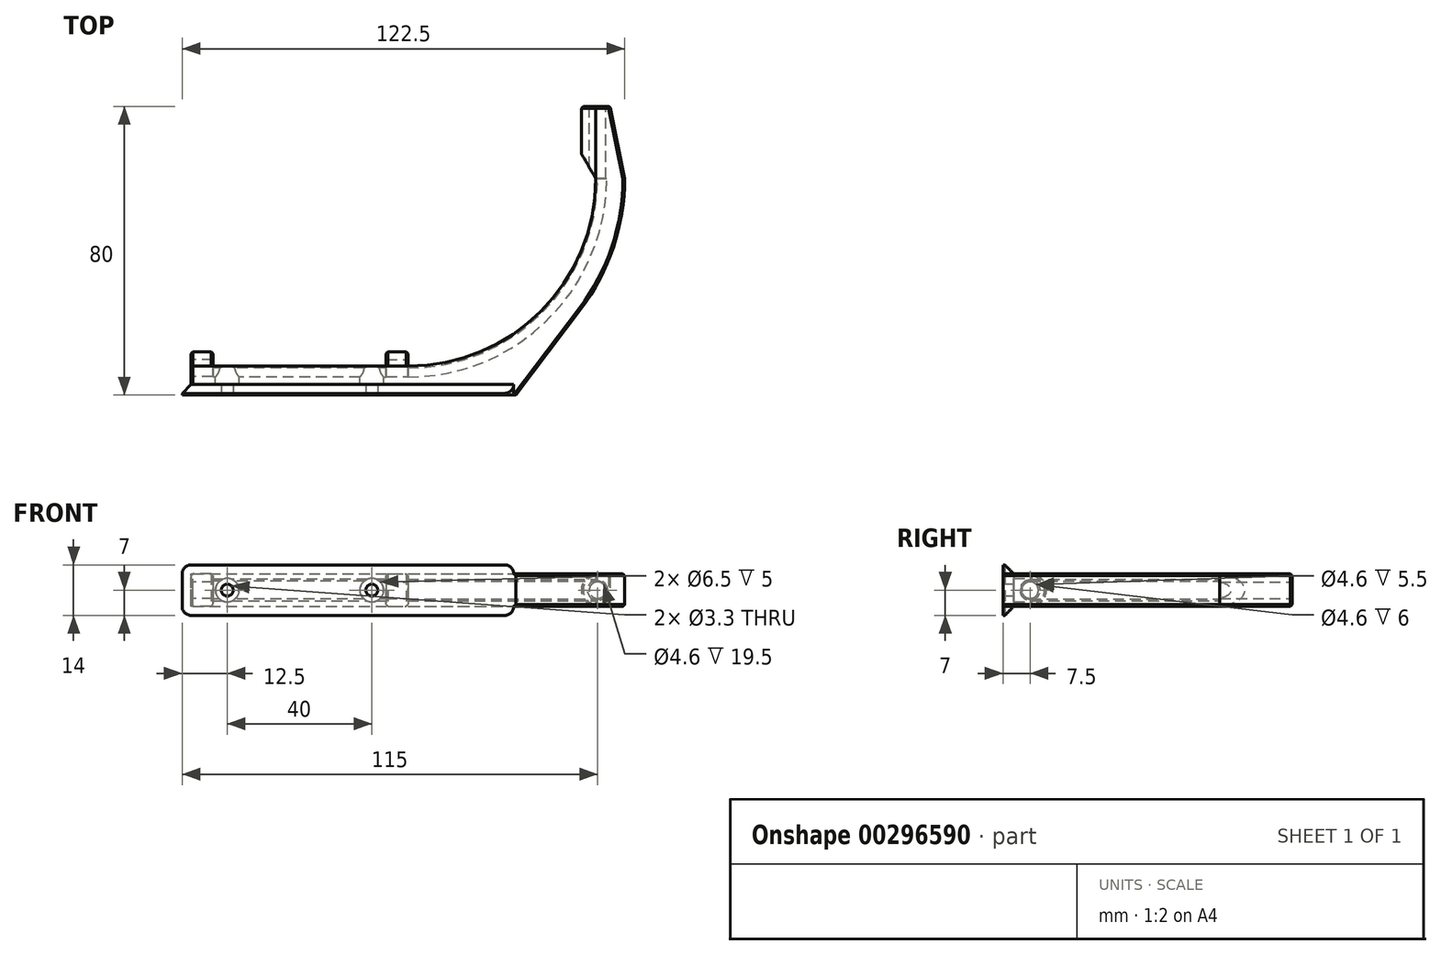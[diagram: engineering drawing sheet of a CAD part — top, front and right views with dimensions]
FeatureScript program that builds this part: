
annotation { "Feature Type Name" : "Feature", "Feature Type Description" : "" }
export const myFeature = defineFeature(function(context is Context, id is Id, definition is map)
    precondition{}
    {
        {
            var Q0;
            Q0=qCreatedBy(makeId("Top.planeOp"),FACE);
            var sketch = newSketch(context, id + "F0", { "sketchPlane" : qUnion([Q0])});
            skCircle(sketch, "E0", {"center": v(0, 120) * mm, "radius": 67 * mm, "construction": true});
            skLineSegment(sketch, "E1", {"start": v(0, 0) * mm, "end": v(0, 120) * mm, "construction": true});
            skLineSegment(sketch, "E2", {"start": v(0, 0) * mm, "end": v(-40, 0) * mm, "construction": true});
            skLineSegment(sketch, "E3", {"start": v(0, 0) * mm, "end": v(40, 0) * mm, "construction": true});
            skCircle(sketch, "E4", {"center": v(0, 120) * mm, "radius": 100 * mm, "construction": true});
            skLineSegment(sketch, "E5", {"start": v(0, 0) * mm, "end": v(50, 0) * mm});
            skArc(sketch, "E6", {"start": v(97.92, 23.9) * mm, "mid": v(106.9, 40.96) * mm, "end": v(110, 60) * mm});
            skLineSegment(sketch, "E7", {"start": v(110, 60) * mm, "end": v(110, 80) * mm});
            skLineSegment(sketch, "E8", {"start": v(0, 0) * mm, "end": v(-10, 0) * mm});
            skLineSegment(sketch, "E9.0", {"start": v(105, 60) * mm, "end": v(105, 80) * mm});
            skArc(sketch, "E9.1", {"start": v(50, 5) * mm, "mid": v(88.9, 21.1) * mm, "end": v(105, 60) * mm});
            skLineSegment(sketch, "E9.2", {"start": v(0, 5) * mm, "end": v(50, 5) * mm});
            skLineSegment(sketch, "E9.3", {"start": v(0, 5) * mm, "end": v(-10, 5) * mm});
            skLineSegment(sketch, "E10", {"start": v(-10, 5) * mm, "end": v(-10, 0) * mm});
            skLineSegment(sketch, "E11", {"start": v(105, 80) * mm, "end": v(110, 80) * mm});
            skLineSegment(sketch, "E12", {"start": v(97.92, 23.9) * mm, "end": v(79.91, 0) * mm});
            skLineSegment(sketch, "E13", {"start": v(50, 0) * mm, "end": v(79.91, 0) * mm});
            skSolve(sketch);
        }
        {
            var Q0;
            Q0 = qSketchRegion(id + "F0", true);
            extrude(context, id + "F1", {"entities" : qUnion([Q0]), "endBound" : BoundingType.SYMMETRIC, "depth" : 9 * mm});
        }
        {
            var Q0;
            Q0=makeQuery(id+"F1.opExtrude","SWEPT_FACE",FACE,{"disambiguationData":[OSD([sQuery(id+"F0.wireOp",EDGE,"E9.2"),sQuery(id+"F0.wireOp",EDGE,"E9.3")])]});
            var sketch = newSketch(context, id + "F2", { "sketchPlane" : qUnion([Q0])});
            skLineSegment(sketch, "E14", {"start": v(0, 0) * mm, "end": v(-40, 0) * mm, "construction": true});
            skPoint(sketch, "E15", {"position": v(-40, 0) * mm});
            skSolve(sketch);
        }
        {
            var Q0;
            Q0=sQuery(id+"F2.wireOp",VERTEX,"E15");
            var Q1;
            Q1=sQuery(id+"F2.wireOp",VERTEX,"E14.start");
            var Q2;
            Q2=makeQuery(id+"F1.opExtrude","SWEPT_BODY",BODY,{"disambiguationData":[OSD([sQuery(id+"F0.wireOp",EDGE,"E5"),sQuery(id+"F0.wireOp",EDGE,"E6"),sQuery(id+"F0.wireOp",EDGE,"E7"),sQuery(id+"F0.wireOp",EDGE,"E8"),sQuery(id+"F0.wireOp",EDGE,"E9.0"),sQuery(id+"F0.wireOp",EDGE,"E9.1"),sQuery(id+"F0.wireOp",EDGE,"E9.2"),sQuery(id+"F0.wireOp",EDGE,"E9.3"),sQuery(id+"F0.wireOp",EDGE,"E10"),sQuery(id+"F0.wireOp",EDGE,"E11")])]});
            hole(context, id + "F3", {"style" : HoleStyle.C_BORE, "endStyle" : HoleEndStyle.THROUGH, "standardTappedOrClearance" : lookupTablePath({ "standard" : "ISO", "fit" : "Normal", "size" : "M3", "type" : "Clearance" }), "standardBlindInLast" : lookupTablePath({ "fit" : "Standard", "standard" : "ISO", "size" : "M3", "type" : "Clearance" }), "holeDiameter" : 3.3 * mm, "cBoreDiameter" : 6.5 * mm, "cBoreDepth" : 3 * mm, "tappedDepth" : 3 * mm, "tapClearance" : 3, "startFromSketch" : true, "locations" : qUnion([Q0, Q1]), "scope" : qUnion([Q2])});
        }
        {
            var Q0;
            Q0=qCreatedBy(makeId("Top.planeOp"),FACE);
            var sketch = newSketch(context, id + "F4", { "sketchPlane" : qUnion([Q0])});
            skLineSegment(sketch, "E16", {"start": v(0, 0) * mm, "end": v(0, 5) * mm, "construction": true});
            skLineSegment(sketch, "E17", {"start": v(0, 5) * mm, "end": v(-10, 5) * mm});
            skLineSegment(sketch, "E18", {"start": v(-10, 5) * mm, "end": v(-10, 8) * mm});
            skLineSegment(sketch, "E19", {"start": v(0, 5) * mm, "end": v(50, 5) * mm});
            skArc(sketch, "E20", {"start": v(50, 5) * mm, "mid": v(88.9, 21.1) * mm, "end": v(105, 60) * mm});
            skLineSegment(sketch, "E21", {"start": v(105, 60) * mm, "end": v(105, 80) * mm});
            skLineSegment(sketch, "E22.0", {"start": v(102, 60) * mm, "end": v(102, 80) * mm});
            skArc(sketch, "E22.1", {"start": v(50, 8) * mm, "mid": v(86.77, 23.23) * mm, "end": v(102, 60) * mm});
            skLineSegment(sketch, "E22.2", {"start": v(0, 8) * mm, "end": v(50, 8) * mm});
            skLineSegment(sketch, "E22.3", {"start": v(0, 8) * mm, "end": v(-10, 8) * mm});
            skLineSegment(sketch, "E23", {"start": v(105, 80) * mm, "end": v(102, 80) * mm});
            skSolve(sketch);
        }
        {
            var Q0;
            Q0 = qSketchRegion(id + "F4", true);
            extrude(context, id + "F5", {"entities" : qUnion([Q0]), "operationType" : NewBodyOperationType.ADD, "endBound" : BoundingType.SYMMETRIC, "depth" : 9 * mm});
        }
        {
            var Q0;
            Q0=qCreatedBy(makeId("Top.planeOp"),FACE);
            var sketch = newSketch(context, id + "F6", { "sketchPlane" : qUnion([Q0])});
            skLineSegment(sketch, "E24", {"start": v(0, 0) * mm, "end": v(0, 5) * mm, "construction": true});
            skLineSegment(sketch, "E25", {"start": v(0, 5) * mm, "end": v(-11, 5) * mm});
            skLineSegment(sketch, "E26", {"start": v(0, 5) * mm, "end": v(50, 5) * mm});
            skArc(sketch, "E27", {"start": v(50, 5) * mm, "mid": v(88.9, 21.1) * mm, "end": v(105, 60) * mm});
            skLineSegment(sketch, "E28", {"start": v(105, 60) * mm, "end": v(105, 81) * mm});
            skLineSegment(sketch, "E29.0", {"start": v(0, 11) * mm, "end": v(-11, 11) * mm});
            skLineSegment(sketch, "E29.1", {"start": v(0, 11) * mm, "end": v(50, 11) * mm});
            skArc(sketch, "E29.2", {"start": v(50, 11) * mm, "mid": v(84.65, 25.35) * mm, "end": v(99, 60) * mm});
            skLineSegment(sketch, "E29.3", {"start": v(99, 60) * mm, "end": v(99, 81) * mm});
            skLineSegment(sketch, "E30", {"start": v(-11, 5) * mm, "end": v(-11, 11) * mm});
            skLineSegment(sketch, "E31", {"start": v(99, 81) * mm, "end": v(105, 81) * mm});
            skSolve(sketch);
        }
        {
            var Q0;
            Q0 = qSketchRegion(id + "F6", true);
            extrude(context, id + "F7", {"entities" : qUnion([Q0]), "operationType" : NewBodyOperationType.REMOVE, "endBound" : BoundingType.SYMMETRIC, "oppositeDirection" : true, "depth" : 5 * mm});
        }
        {
            var Q0;
            Q0=makeQuery(id+"F5.boolean.opBoolean","MERGE",FACE,{"derivedFrom":[makeQuery(id+"F1.opExtrude","SWEPT_FACE",FACE,{"disambiguationData":[OSD([sQuery(id+"F0.wireOp",EDGE,"E10")])]}),makeQuery(id+"F5.opExtrude","SWEPT_FACE",FACE,{"disambiguationData":[OSD([sQuery(id+"F4.wireOp",EDGE,"E18")])]})]});
            var sketch = newSketch(context, id + "F8", { "sketchPlane" : qUnion([Q0])});
            skLineSegment(sketch, "E32", {"start": v(0, 0) * mm, "end": v(-7.5, 0) * mm, "construction": true});
            skPoint(sketch, "E32.endSnap0", {"position": v(-5, 0) * mm});
            skCircle(sketch, "E33", {"center": v(-7.5, 0) * mm, "radius": 2.3 * mm});
            skCircle(sketch, "E34", {"center": v(-7.5, 0) * mm, "radius": 4.5 * mm});
            skSolve(sketch);
        }
        {
            var Q0;
            Q0 = qSketchRegion(id + "F8", true);
            extrude(context, id + "F9", {"entities" : qUnion([Q0]), "operationType" : NewBodyOperationType.ADD, "oppositeDirection" : true, "depth" : 6 * mm});
        }
        {
            var Q0;
            Q0=makeQuery(id+"F5.boolean.opBoolean","MERGE",FACE,{"derivedFrom":[makeQuery(id+"F1.opExtrude","SWEPT_FACE",FACE,{"disambiguationData":[OSD([sQuery(id+"F0.wireOp",EDGE,"E11")])]}),makeQuery(id+"F5.opExtrude","SWEPT_FACE",FACE,{"disambiguationData":[OSD([sQuery(id+"F4.wireOp",EDGE,"E23")])]})]});
            var sketch = newSketch(context, id + "F10", { "sketchPlane" : qUnion([Q0])});
            skLineSegment(sketch, "E35", {"start": v(-110, 0) * mm, "end": v(-102.5, 0) * mm, "construction": true});
            skPoint(sketch, "E35.endSnap0", {"position": v(-105, 0) * mm});
            skCircle(sketch, "E36", {"center": v(-102.5, 0) * mm, "radius": 2.3 * mm});
            skCircle(sketch, "E37", {"center": v(-102.5, 0) * mm, "radius": 4.5 * mm});
            skSolve(sketch);
        }
        {
            var Q0;
            Q0 = qSketchRegion(id + "F10", true);
            extrude(context, id + "F11", {"entities" : qUnion([Q0]), "operationType" : NewBodyOperationType.ADD, "oppositeDirection" : true, "depth" : 20 * mm});
        }
        {
            var Q0;
            Q0=makeQuery(id+"F7.boolean.opBoolean","INTERSECT",VERTEX,{"derivedFrom":[makeQuery(id+"F5.opExtrude","SWEPT_FACE",FACE,{"disambiguationData":[OSD([sQuery(id+"F4.wireOp",EDGE,"E22.1")])]}),makeQuery(id+"F5.opExtrude","SWEPT_FACE",FACE,{"disambiguationData":[OSD([sQuery(id+"F4.wireOp",EDGE,"E22.2"),sQuery(id+"F4.wireOp",EDGE,"E22.3")])]}),makeQuery(id+"F7.opExtrude","CAP_FACE",FACE,{"disambiguationData":[OSD([sQuery(id+"F6.wireOp",EDGE,"E25"),sQuery(id+"F6.wireOp",EDGE,"E26"),sQuery(id+"F6.wireOp",EDGE,"E27"),sQuery(id+"F6.wireOp",EDGE,"E28"),sQuery(id+"F6.wireOp",EDGE,"E29.0"),sQuery(id+"F6.wireOp",EDGE,"E29.1"),sQuery(id+"F6.wireOp",EDGE,"E29.2"),sQuery(id+"F6.wireOp",EDGE,"E29.3"),sQuery(id+"F6.wireOp",EDGE,"E30"),sQuery(id+"F6.wireOp",EDGE,"E31")])],"isStart":false})]});
            var Q1;
            Q1=makeQuery(id+"F7.boolean.opBoolean","INTERSECT",VERTEX,{"derivedFrom":[makeQuery(id+"F5.opExtrude","SWEPT_FACE",FACE,{"disambiguationData":[OSD([sQuery(id+"F4.wireOp",EDGE,"E22.1")])]}),makeQuery(id+"F5.opExtrude","SWEPT_FACE",FACE,{"disambiguationData":[OSD([sQuery(id+"F4.wireOp",EDGE,"E22.2"),sQuery(id+"F4.wireOp",EDGE,"E22.3")])]}),makeQuery(id+"F7.opExtrude","CAP_FACE",FACE,{"disambiguationData":[OSD([sQuery(id+"F6.wireOp",EDGE,"E25"),sQuery(id+"F6.wireOp",EDGE,"E26"),sQuery(id+"F6.wireOp",EDGE,"E27"),sQuery(id+"F6.wireOp",EDGE,"E28"),sQuery(id+"F6.wireOp",EDGE,"E29.0"),sQuery(id+"F6.wireOp",EDGE,"E29.1"),sQuery(id+"F6.wireOp",EDGE,"E29.2"),sQuery(id+"F6.wireOp",EDGE,"E29.3"),sQuery(id+"F6.wireOp",EDGE,"E30"),sQuery(id+"F6.wireOp",EDGE,"E31")])],"isStart":true})]});
            var Q2;
            Q2=makeQuery(id+"F7.boolean.opBoolean","COPY",VERTEX,{"derivedFrom":makeQuery(id+"F7.opExtrude","CAP_VERTEX",VERTEX,{"disambiguationData":[OSD([sQuery(id+"F6.wireOp",EDGE,"E26"),sQuery(id+"F6.wireOp",EDGE,"E27")])],"isStart":false})});
            cPlane(context, id + "F12", {"entities" : qUnion([Q0, Q1, Q2]), "cplaneType" : CPlaneType.THREE_POINT, "offset" : 25 * mm, "width" : 150 * mm, "height" : 150 * mm});
        }
        {
            var Q0;
            Q0=qCreatedBy(id+"F12.planeOp",FACE);
            var sketch = newSketch(context, id + "F13", { "sketchPlane" : qUnion([Q0])});
            skLineSegment(sketch, "E38", {"start": v(-7.5, 0) * mm, "end": v(0, 0) * mm, "construction": true});
            skCircle(sketch, "E39", {"center": v(-7.5, 0) * mm, "radius": 2.3 * mm});
            skCircle(sketch, "E40", {"center": v(-7.5, 0) * mm, "radius": 4.5 * mm});
            skSolve(sketch);
        }
        {
            var Q0;
            Q0 = qSketchRegion(id + "F13", true);
            extrude(context, id + "F14", {"entities" : qUnion([Q0]), "operationType" : NewBodyOperationType.ADD, "depth" : 6 * mm});
        }
        {
            var Q0;
            {var subQ1=sQuery(id+"F0.wireOp",EDGE,"E10");var subQ2=sQuery(id+"F4.wireOp",EDGE,"E22.3");var subQ3=sQuery(id+"F4.wireOp",EDGE,"E22.2");Q0=makeQuery(id+"F7.boolean.opBoolean","SPLIT",FACE,{"disambiguationData":[TD([makeQuery(id+"F1.opExtrude","CAP_FACE",FACE,{"disambiguationData":[OSD([sQuery(id+"F0.wireOp",EDGE,"E5"),sQuery(id+"F0.wireOp",EDGE,"E6"),sQuery(id+"F0.wireOp",EDGE,"E7"),sQuery(id+"F0.wireOp",EDGE,"E8"),sQuery(id+"F0.wireOp",EDGE,"E9.0"),sQuery(id+"F0.wireOp",EDGE,"E9.1"),sQuery(id+"F0.wireOp",EDGE,"E9.2"),sQuery(id+"F0.wireOp",EDGE,"E9.3"),subQ1,sQuery(id+"F0.wireOp",EDGE,"E11")])],"isStart":true})])],"derivedFrom":makeQuery(id+"F5.opExtrude","SWEPT_FACE",FACE,{"disambiguationData":[OSD([subQ3,subQ2])]})});}
            var sketch = newSketch(context, id + "F15", { "sketchPlane" : qUnion([Q0])});
            skLineSegment(sketch, "E41", {"start": v(0, 0) * mm, "end": v(-40, 0) * mm, "construction": true});
            skCircle(sketch, "E42", {"center": v(-40, 0) * mm, "radius": 3.25 * mm});
            skCircle(sketch, "E43", {"center": v(0, 0) * mm, "radius": 3.25 * mm});
            skSolve(sketch);
        }
        {
            var Q0;
            Q0 = qSketchRegion(id + "F15", true);
            extrude(context, id + "F16", {"entities" : qUnion([Q0]), "operationType" : NewBodyOperationType.REMOVE, "oppositeDirection" : true, "depth" : 3 * mm});
        }
        {
            var Q0;
            Q0=makeQuery(id+"F5.boolean.opBoolean","MERGE",FACE,{"derivedFrom":[makeQuery(id+"F1.opExtrude","CAP_FACE",FACE,{"disambiguationData":[OSD([sQuery(id+"F0.wireOp",EDGE,"E5"),sQuery(id+"F0.wireOp",EDGE,"E6"),sQuery(id+"F0.wireOp",EDGE,"E7"),sQuery(id+"F0.wireOp",EDGE,"E8"),sQuery(id+"F0.wireOp",EDGE,"E9.0"),sQuery(id+"F0.wireOp",EDGE,"E9.1"),sQuery(id+"F0.wireOp",EDGE,"E9.2"),sQuery(id+"F0.wireOp",EDGE,"E9.3"),sQuery(id+"F0.wireOp",EDGE,"E10"),sQuery(id+"F0.wireOp",EDGE,"E11"),sQuery(id+"F0.wireOp",EDGE,"E12"),sQuery(id+"F0.wireOp",EDGE,"E13")])],"isStart":false}),makeQuery(id+"F5.opExtrude","CAP_FACE",FACE,{"disambiguationData":[OSD([sQuery(id+"F4.wireOp",EDGE,"E17"),sQuery(id+"F4.wireOp",EDGE,"E18"),sQuery(id+"F4.wireOp",EDGE,"E19"),sQuery(id+"F4.wireOp",EDGE,"E20"),sQuery(id+"F4.wireOp",EDGE,"E21"),sQuery(id+"F4.wireOp",EDGE,"E22.0"),sQuery(id+"F4.wireOp",EDGE,"E22.1"),sQuery(id+"F4.wireOp",EDGE,"E22.2"),sQuery(id+"F4.wireOp",EDGE,"E22.3"),sQuery(id+"F4.wireOp",EDGE,"E23")])],"isStart":false})]});
            var sketch = newSketch(context, id + "F17", { "sketchPlane" : qUnion([Q0])});
            skLineSegment(sketch, "E44", {"start": v(0, 0) * mm, "end": v(102, 0) * mm, "construction": true});
            skLineSegment(sketch, "E45", {"start": v(102, 0) * mm, "end": v(102, 60) * mm, "construction": true});
            skLineSegment(sketch, "E46", {"start": v(102, 60) * mm, "end": v(96, 60) * mm});
            skLineSegment(sketch, "E47", {"start": v(96, 60) * mm, "end": v(96, 70.4) * mm});
            skLineSegment(sketch, "E48", {"start": v(96, 70.4) * mm, "end": v(102, 60) * mm});
            skSolve(sketch);
        }
        {
            var Q0;
            Q0 = qSketchRegion(id + "F17", true);
            extrude(context, id + "F18", {"entities" : qUnion([Q0]), "operationType" : NewBodyOperationType.REMOVE, "endBound" : BoundingType.THROUGH_ALL, "oppositeDirection" : true, "depth" : 25 * mm});
        }
        {
            var Q0;
            {var subQ0=sQuery(id+"F6.wireOp",EDGE,"E27");var subQ1=sQuery(id+"F6.wireOp",EDGE,"E26");var subQ2=sQuery(id+"F6.wireOp",EDGE,"E25");var subQ3=makeQuery(id+"F7.opExtrude","CAP_FACE",FACE,{"disambiguationData":[OSD([subQ2,subQ1,subQ0,sQuery(id+"F6.wireOp",EDGE,"E28"),sQuery(id+"F6.wireOp",EDGE,"E29.0"),sQuery(id+"F6.wireOp",EDGE,"E29.1"),sQuery(id+"F6.wireOp",EDGE,"E29.2"),sQuery(id+"F6.wireOp",EDGE,"E29.3"),sQuery(id+"F6.wireOp",EDGE,"E30"),sQuery(id+"F6.wireOp",EDGE,"E31")])],"isStart":false});var subQ4=makeQuery(id+"F7.opExtrude","SWEPT_FACE",FACE,{"disambiguationData":[OSD([subQ2,subQ1])]});Q0=makeQuery(id+"F7.boolean.opBoolean","COPY",EDGE,{"disambiguationData":[topologyDisambiguationEdgeConnected([subQ4,subQ3]),TD([makeQuery(id+"F3.hole-0.boolean.opBoolean","COPY",FACE,{"derivedFrom":makeQuery(id+"F3.hole-0.opRevolve","SWEPT_FACE",FACE,{"disambiguationData":[OSD([sQuery(id+"F3.hole-0.sketch.wireOp",EDGE,"cbore_start_line_2")])]})}),makeQuery(id+"F5.opExtrude","SWEPT_FACE",FACE,{"disambiguationData":[OSD([sQuery(id+"F4.wireOp",EDGE,"E17"),sQuery(id+"F4.wireOp",EDGE,"E19")])]}),subQ4,subQ3,makeQuery(id+"F7.opExtrude","SWEPT_FACE",FACE,{"disambiguationData":[OSD([subQ0])]})])],"derivedFrom":makeQuery(id+"F7.opExtrude","CAP_EDGE",EDGE,{"disambiguationData":[OSD([subQ2,subQ1])],"isStart":false})});}
            var Q1;
            {var subQ0=sQuery(id+"F6.wireOp",EDGE,"E27");var subQ1=sQuery(id+"F6.wireOp",EDGE,"E26");var subQ2=sQuery(id+"F6.wireOp",EDGE,"E25");var subQ3=makeQuery(id+"F7.opExtrude","CAP_FACE",FACE,{"disambiguationData":[OSD([subQ2,subQ1,subQ0,sQuery(id+"F6.wireOp",EDGE,"E28"),sQuery(id+"F6.wireOp",EDGE,"E29.0"),sQuery(id+"F6.wireOp",EDGE,"E29.1"),sQuery(id+"F6.wireOp",EDGE,"E29.2"),sQuery(id+"F6.wireOp",EDGE,"E29.3"),sQuery(id+"F6.wireOp",EDGE,"E30"),sQuery(id+"F6.wireOp",EDGE,"E31")])],"isStart":true});var subQ4=makeQuery(id+"F7.opExtrude","SWEPT_FACE",FACE,{"disambiguationData":[OSD([subQ2,subQ1])]});Q1=makeQuery(id+"F7.boolean.opBoolean","COPY",EDGE,{"disambiguationData":[topologyDisambiguationEdgeConnected([subQ4,subQ3]),TD([makeQuery(id+"F3.hole-0.boolean.opBoolean","COPY",FACE,{"derivedFrom":makeQuery(id+"F3.hole-0.opRevolve","SWEPT_FACE",FACE,{"disambiguationData":[OSD([sQuery(id+"F3.hole-0.sketch.wireOp",EDGE,"cbore_start_line_2")])]})}),makeQuery(id+"F5.opExtrude","SWEPT_FACE",FACE,{"disambiguationData":[OSD([sQuery(id+"F4.wireOp",EDGE,"E17"),sQuery(id+"F4.wireOp",EDGE,"E19")])]}),subQ4,subQ3,makeQuery(id+"F7.opExtrude","SWEPT_FACE",FACE,{"disambiguationData":[OSD([subQ0])]})])],"derivedFrom":makeQuery(id+"F7.opExtrude","CAP_EDGE",EDGE,{"disambiguationData":[OSD([subQ2,subQ1])],"isStart":true})});}
            var Q2;
            {var subQ0=sQuery(id+"F6.wireOp",EDGE,"E26");var subQ1=sQuery(id+"F6.wireOp",EDGE,"E25");var subQ2=makeQuery(id+"F7.opExtrude","SWEPT_FACE",FACE,{"disambiguationData":[OSD([subQ1,subQ0])]});var subQ3=makeQuery(id+"F7.opExtrude","CAP_FACE",FACE,{"disambiguationData":[OSD([subQ1,subQ0,sQuery(id+"F6.wireOp",EDGE,"E27"),sQuery(id+"F6.wireOp",EDGE,"E28"),sQuery(id+"F6.wireOp",EDGE,"E29.0"),sQuery(id+"F6.wireOp",EDGE,"E29.1"),sQuery(id+"F6.wireOp",EDGE,"E29.2"),sQuery(id+"F6.wireOp",EDGE,"E29.3"),sQuery(id+"F6.wireOp",EDGE,"E30"),sQuery(id+"F6.wireOp",EDGE,"E31")])],"isStart":false});Q2=makeQuery(id+"F7.boolean.opBoolean","COPY",EDGE,{"disambiguationData":[topologyDisambiguationEdgeConnected([subQ2,subQ3]),TD([makeQuery(id+"F3.hole-0.boolean.opBoolean","COPY",FACE,{"derivedFrom":makeQuery(id+"F3.hole-0.opRevolve","SWEPT_FACE",FACE,{"disambiguationData":[OSD([sQuery(id+"F3.hole-0.sketch.wireOp",EDGE,"cbore_start_line_2")])]})}),makeQuery(id+"F3.hole-1.boolean.opBoolean","COPY",FACE,{"derivedFrom":makeQuery(id+"F3.hole-1.opRevolve","SWEPT_FACE",FACE,{"disambiguationData":[OSD([sQuery(id+"F3.hole-1.sketch.wireOp",EDGE,"cbore_start_line_2")])]})}),makeQuery(id+"F5.opExtrude","SWEPT_FACE",FACE,{"disambiguationData":[OSD([sQuery(id+"F4.wireOp",EDGE,"E17"),sQuery(id+"F4.wireOp",EDGE,"E19")])]}),subQ2,subQ3])],"derivedFrom":makeQuery(id+"F7.opExtrude","CAP_EDGE",EDGE,{"disambiguationData":[OSD([subQ1,subQ0])],"isStart":false})});}
            var Q3;
            {var subQ0=sQuery(id+"F6.wireOp",EDGE,"E26");var subQ1=sQuery(id+"F6.wireOp",EDGE,"E25");var subQ2=makeQuery(id+"F7.opExtrude","SWEPT_FACE",FACE,{"disambiguationData":[OSD([subQ1,subQ0])]});var subQ3=makeQuery(id+"F7.opExtrude","CAP_FACE",FACE,{"disambiguationData":[OSD([subQ1,subQ0,sQuery(id+"F6.wireOp",EDGE,"E27"),sQuery(id+"F6.wireOp",EDGE,"E28"),sQuery(id+"F6.wireOp",EDGE,"E29.0"),sQuery(id+"F6.wireOp",EDGE,"E29.1"),sQuery(id+"F6.wireOp",EDGE,"E29.2"),sQuery(id+"F6.wireOp",EDGE,"E29.3"),sQuery(id+"F6.wireOp",EDGE,"E30"),sQuery(id+"F6.wireOp",EDGE,"E31")])],"isStart":true});Q3=makeQuery(id+"F7.boolean.opBoolean","COPY",EDGE,{"disambiguationData":[topologyDisambiguationEdgeConnected([subQ2,subQ3]),TD([makeQuery(id+"F3.hole-0.boolean.opBoolean","COPY",FACE,{"derivedFrom":makeQuery(id+"F3.hole-0.opRevolve","SWEPT_FACE",FACE,{"disambiguationData":[OSD([sQuery(id+"F3.hole-0.sketch.wireOp",EDGE,"cbore_start_line_2")])]})}),makeQuery(id+"F3.hole-1.boolean.opBoolean","COPY",FACE,{"derivedFrom":makeQuery(id+"F3.hole-1.opRevolve","SWEPT_FACE",FACE,{"disambiguationData":[OSD([sQuery(id+"F3.hole-1.sketch.wireOp",EDGE,"cbore_start_line_2")])]})}),makeQuery(id+"F5.opExtrude","SWEPT_FACE",FACE,{"disambiguationData":[OSD([sQuery(id+"F4.wireOp",EDGE,"E17"),sQuery(id+"F4.wireOp",EDGE,"E19")])]}),subQ2,subQ3])],"derivedFrom":makeQuery(id+"F7.opExtrude","CAP_EDGE",EDGE,{"disambiguationData":[OSD([subQ1,subQ0])],"isStart":true})});}
            var Q4;
            {var subQ0=sQuery(id+"F6.wireOp",EDGE,"E26");var subQ1=sQuery(id+"F6.wireOp",EDGE,"E25");var subQ2=makeQuery(id+"F7.opExtrude","CAP_FACE",FACE,{"disambiguationData":[OSD([subQ1,subQ0,sQuery(id+"F6.wireOp",EDGE,"E27"),sQuery(id+"F6.wireOp",EDGE,"E28"),sQuery(id+"F6.wireOp",EDGE,"E29.0"),sQuery(id+"F6.wireOp",EDGE,"E29.1"),sQuery(id+"F6.wireOp",EDGE,"E29.2"),sQuery(id+"F6.wireOp",EDGE,"E29.3"),sQuery(id+"F6.wireOp",EDGE,"E30"),sQuery(id+"F6.wireOp",EDGE,"E31")])],"isStart":false});var subQ3=makeQuery(id+"F7.opExtrude","SWEPT_FACE",FACE,{"disambiguationData":[OSD([subQ1,subQ0])]});Q4=makeQuery(id+"F7.boolean.opBoolean","COPY",EDGE,{"disambiguationData":[topologyDisambiguationEdgeConnected([subQ3,subQ2]),TD([makeQuery(id+"F1.opExtrude","SWEPT_FACE",FACE,{"disambiguationData":[OSD([sQuery(id+"F0.wireOp",EDGE,"E10")])]}),makeQuery(id+"F3.hole-1.boolean.opBoolean","COPY",FACE,{"derivedFrom":makeQuery(id+"F3.hole-1.opRevolve","SWEPT_FACE",FACE,{"disambiguationData":[OSD([sQuery(id+"F3.hole-1.sketch.wireOp",EDGE,"cbore_start_line_2")])]})}),makeQuery(id+"F5.opExtrude","SWEPT_FACE",FACE,{"disambiguationData":[OSD([sQuery(id+"F4.wireOp",EDGE,"E17"),sQuery(id+"F4.wireOp",EDGE,"E19")])]}),makeQuery(id+"F5.opExtrude","SWEPT_FACE",FACE,{"disambiguationData":[OSD([sQuery(id+"F4.wireOp",EDGE,"E18")])]}),subQ3,subQ2])],"derivedFrom":makeQuery(id+"F7.opExtrude","CAP_EDGE",EDGE,{"disambiguationData":[OSD([subQ1,subQ0])],"isStart":false})});}
            var Q5;
            {var subQ0=sQuery(id+"F6.wireOp",EDGE,"E26");var subQ1=sQuery(id+"F6.wireOp",EDGE,"E25");var subQ2=makeQuery(id+"F7.opExtrude","SWEPT_FACE",FACE,{"disambiguationData":[OSD([subQ1,subQ0])]});var subQ3=makeQuery(id+"F7.opExtrude","CAP_FACE",FACE,{"disambiguationData":[OSD([subQ1,subQ0,sQuery(id+"F6.wireOp",EDGE,"E27"),sQuery(id+"F6.wireOp",EDGE,"E28"),sQuery(id+"F6.wireOp",EDGE,"E29.0"),sQuery(id+"F6.wireOp",EDGE,"E29.1"),sQuery(id+"F6.wireOp",EDGE,"E29.2"),sQuery(id+"F6.wireOp",EDGE,"E29.3"),sQuery(id+"F6.wireOp",EDGE,"E30"),sQuery(id+"F6.wireOp",EDGE,"E31")])],"isStart":true});Q5=makeQuery(id+"F7.boolean.opBoolean","COPY",EDGE,{"disambiguationData":[topologyDisambiguationEdgeConnected([subQ2,subQ3]),TD([makeQuery(id+"F1.opExtrude","SWEPT_FACE",FACE,{"disambiguationData":[OSD([sQuery(id+"F0.wireOp",EDGE,"E10")])]}),makeQuery(id+"F3.hole-1.boolean.opBoolean","COPY",FACE,{"derivedFrom":makeQuery(id+"F3.hole-1.opRevolve","SWEPT_FACE",FACE,{"disambiguationData":[OSD([sQuery(id+"F3.hole-1.sketch.wireOp",EDGE,"cbore_start_line_2")])]})}),makeQuery(id+"F5.opExtrude","SWEPT_FACE",FACE,{"disambiguationData":[OSD([sQuery(id+"F4.wireOp",EDGE,"E17"),sQuery(id+"F4.wireOp",EDGE,"E19")])]}),makeQuery(id+"F5.opExtrude","SWEPT_FACE",FACE,{"disambiguationData":[OSD([sQuery(id+"F4.wireOp",EDGE,"E18")])]}),subQ2,subQ3])],"derivedFrom":makeQuery(id+"F7.opExtrude","CAP_EDGE",EDGE,{"disambiguationData":[OSD([subQ1,subQ0])],"isStart":true})});}
            var Q6;
            Q6=makeQuery(id+"F7.boolean.opBoolean","COPY",EDGE,{"derivedFrom":makeQuery(id+"F7.opExtrude","CAP_EDGE",EDGE,{"disambiguationData":[OSD([sQuery(id+"F6.wireOp",EDGE,"E27")])],"isStart":true})});
            var Q7;
            Q7=makeQuery(id+"F7.boolean.opBoolean","COPY",EDGE,{"derivedFrom":makeQuery(id+"F7.opExtrude","CAP_EDGE",EDGE,{"disambiguationData":[OSD([sQuery(id+"F6.wireOp",EDGE,"E27")])],"isStart":false})});
            fillet(context, id + "F19", {"entities" : qUnion([Q0, Q1, Q2, Q3, Q4, Q5, Q6, Q7]), "radius" : 2.5 * mm, "tangentPropagation" : true, "allowEdgeOverflow" : false});
        }
        {
            var Q0;
            Q0=makeQuery(id+"F1.opExtrude","SWEPT_EDGE",EDGE,{"disambiguationData":[OSD([sQuery(id+"F0.wireOp",EDGE,"E7"),sQuery(id+"F0.wireOp",EDGE,"E11")])]});
            chamfer(context, id + "F20", {"entities" : qUnion([Q0]), "chamferType" : ChamferType.TWO_OFFSETS, "width1" : 4 * mm, "oppositeDirection" : false, "width2" : 20 * mm, "tangentPropagation" : true});
        }
        {
            var Q0;
            Q0=makeQuery(id+"F9.opExtrude","CAP_EDGE",EDGE,{"disambiguationData":[OSD([sQuery(id+"F8.wireOp",EDGE,"E34")])],"isStart":false});
            var Q1;
            {var subQ0=makeQuery(id+"F7.opExtrude","CAP_FACE",FACE,{"disambiguationData":[OSD([sQuery(id+"F6.wireOp",EDGE,"E25"),sQuery(id+"F6.wireOp",EDGE,"E26"),sQuery(id+"F6.wireOp",EDGE,"E27"),sQuery(id+"F6.wireOp",EDGE,"E28"),sQuery(id+"F6.wireOp",EDGE,"E29.0"),sQuery(id+"F6.wireOp",EDGE,"E29.1"),sQuery(id+"F6.wireOp",EDGE,"E29.2"),sQuery(id+"F6.wireOp",EDGE,"E29.3"),sQuery(id+"F6.wireOp",EDGE,"E30"),sQuery(id+"F6.wireOp",EDGE,"E31")])],"isStart":false});var subQ1=makeQuery(id+"F5.opExtrude","SWEPT_FACE",FACE,{"disambiguationData":[OSD([sQuery(id+"F4.wireOp",EDGE,"E22.2"),sQuery(id+"F4.wireOp",EDGE,"E22.3")])]});Q1=makeQuery(id+"F16.boolean.opBoolean","SPLIT",EDGE,{"disambiguationData":[TD([makeQuery(id+"F3.hole-1.boolean.opBoolean","COPY",FACE,{"derivedFrom":makeQuery(id+"F3.hole-1.opRevolve","SWEPT_FACE",FACE,{"disambiguationData":[OSD([sQuery(id+"F3.hole-1.sketch.wireOp",EDGE,"cbore_start_line_2")])]})}),subQ1,makeQuery(id+"F7.boolean.opBoolean","COPY",FACE,{"derivedFrom":subQ0}),makeQuery(id+"F9.opExtrude","CAP_FACE",FACE,{"disambiguationData":[OSD([sQuery(id+"F8.wireOp",EDGE,"E33"),sQuery(id+"F8.wireOp",EDGE,"E34")])],"isStart":false}),makeQuery(id+"F16.opExtrude","SWEPT_FACE",FACE,{"disambiguationData":[OSD([sQuery(id+"F15.wireOp",EDGE,"E43")])]})])],"derivedFrom":makeQuery(id+"F7.boolean.opBoolean","INTERSECT",EDGE,{"derivedFrom":[subQ1,subQ0]})});}
            var Q2;
            {var subQ0=makeQuery(id+"F7.opExtrude","CAP_FACE",FACE,{"disambiguationData":[OSD([sQuery(id+"F6.wireOp",EDGE,"E25"),sQuery(id+"F6.wireOp",EDGE,"E26"),sQuery(id+"F6.wireOp",EDGE,"E27"),sQuery(id+"F6.wireOp",EDGE,"E28"),sQuery(id+"F6.wireOp",EDGE,"E29.0"),sQuery(id+"F6.wireOp",EDGE,"E29.1"),sQuery(id+"F6.wireOp",EDGE,"E29.2"),sQuery(id+"F6.wireOp",EDGE,"E29.3"),sQuery(id+"F6.wireOp",EDGE,"E30"),sQuery(id+"F6.wireOp",EDGE,"E31")])],"isStart":true});var subQ1=makeQuery(id+"F5.opExtrude","SWEPT_FACE",FACE,{"disambiguationData":[OSD([sQuery(id+"F4.wireOp",EDGE,"E22.2"),sQuery(id+"F4.wireOp",EDGE,"E22.3")])]});Q2=makeQuery(id+"F16.boolean.opBoolean","SPLIT",EDGE,{"disambiguationData":[TD([makeQuery(id+"F3.hole-1.boolean.opBoolean","COPY",FACE,{"derivedFrom":makeQuery(id+"F3.hole-1.opRevolve","SWEPT_FACE",FACE,{"disambiguationData":[OSD([sQuery(id+"F3.hole-1.sketch.wireOp",EDGE,"cbore_start_line_2")])]})}),subQ1,makeQuery(id+"F7.boolean.opBoolean","COPY",FACE,{"derivedFrom":subQ0}),makeQuery(id+"F9.opExtrude","CAP_FACE",FACE,{"disambiguationData":[OSD([sQuery(id+"F8.wireOp",EDGE,"E33"),sQuery(id+"F8.wireOp",EDGE,"E34")])],"isStart":false}),makeQuery(id+"F16.opExtrude","SWEPT_FACE",FACE,{"disambiguationData":[OSD([sQuery(id+"F15.wireOp",EDGE,"E43")])]})])],"derivedFrom":makeQuery(id+"F7.boolean.opBoolean","INTERSECT",EDGE,{"derivedFrom":[subQ1,subQ0]})});}
            var Q3;
            {var subQ0=makeQuery(id+"F7.opExtrude","CAP_FACE",FACE,{"disambiguationData":[OSD([sQuery(id+"F6.wireOp",EDGE,"E25"),sQuery(id+"F6.wireOp",EDGE,"E26"),sQuery(id+"F6.wireOp",EDGE,"E27"),sQuery(id+"F6.wireOp",EDGE,"E28"),sQuery(id+"F6.wireOp",EDGE,"E29.0"),sQuery(id+"F6.wireOp",EDGE,"E29.1"),sQuery(id+"F6.wireOp",EDGE,"E29.2"),sQuery(id+"F6.wireOp",EDGE,"E29.3"),sQuery(id+"F6.wireOp",EDGE,"E30"),sQuery(id+"F6.wireOp",EDGE,"E31")])],"isStart":true});var subQ1=makeQuery(id+"F5.opExtrude","SWEPT_FACE",FACE,{"disambiguationData":[OSD([sQuery(id+"F4.wireOp",EDGE,"E22.2"),sQuery(id+"F4.wireOp",EDGE,"E22.3")])]});Q3=makeQuery(id+"F16.boolean.opBoolean","SPLIT",EDGE,{"disambiguationData":[TD([makeQuery(id+"F3.hole-0.boolean.opBoolean","COPY",FACE,{"derivedFrom":makeQuery(id+"F3.hole-0.opRevolve","SWEPT_FACE",FACE,{"disambiguationData":[OSD([sQuery(id+"F3.hole-0.sketch.wireOp",EDGE,"cbore_start_line_2")])]})}),makeQuery(id+"F3.hole-1.boolean.opBoolean","COPY",FACE,{"derivedFrom":makeQuery(id+"F3.hole-1.opRevolve","SWEPT_FACE",FACE,{"disambiguationData":[OSD([sQuery(id+"F3.hole-1.sketch.wireOp",EDGE,"cbore_start_line_2")])]})}),subQ1,makeQuery(id+"F7.boolean.opBoolean","COPY",FACE,{"derivedFrom":subQ0}),makeQuery(id+"F16.opExtrude","SWEPT_FACE",FACE,{"disambiguationData":[OSD([sQuery(id+"F15.wireOp",EDGE,"E42")])]}),makeQuery(id+"F16.opExtrude","SWEPT_FACE",FACE,{"disambiguationData":[OSD([sQuery(id+"F15.wireOp",EDGE,"E43")])]})])],"derivedFrom":makeQuery(id+"F7.boolean.opBoolean","INTERSECT",EDGE,{"derivedFrom":[subQ1,subQ0]})});}
            var Q4;
            {var subQ0=makeQuery(id+"F7.opExtrude","CAP_FACE",FACE,{"disambiguationData":[OSD([sQuery(id+"F6.wireOp",EDGE,"E25"),sQuery(id+"F6.wireOp",EDGE,"E26"),sQuery(id+"F6.wireOp",EDGE,"E27"),sQuery(id+"F6.wireOp",EDGE,"E28"),sQuery(id+"F6.wireOp",EDGE,"E29.0"),sQuery(id+"F6.wireOp",EDGE,"E29.1"),sQuery(id+"F6.wireOp",EDGE,"E29.2"),sQuery(id+"F6.wireOp",EDGE,"E29.3"),sQuery(id+"F6.wireOp",EDGE,"E30"),sQuery(id+"F6.wireOp",EDGE,"E31")])],"isStart":false});var subQ1=makeQuery(id+"F5.opExtrude","SWEPT_FACE",FACE,{"disambiguationData":[OSD([sQuery(id+"F4.wireOp",EDGE,"E22.2"),sQuery(id+"F4.wireOp",EDGE,"E22.3")])]});Q4=makeQuery(id+"F16.boolean.opBoolean","SPLIT",EDGE,{"disambiguationData":[TD([makeQuery(id+"F3.hole-0.boolean.opBoolean","COPY",FACE,{"derivedFrom":makeQuery(id+"F3.hole-0.opRevolve","SWEPT_FACE",FACE,{"disambiguationData":[OSD([sQuery(id+"F3.hole-0.sketch.wireOp",EDGE,"cbore_start_line_2")])]})}),makeQuery(id+"F3.hole-1.boolean.opBoolean","COPY",FACE,{"derivedFrom":makeQuery(id+"F3.hole-1.opRevolve","SWEPT_FACE",FACE,{"disambiguationData":[OSD([sQuery(id+"F3.hole-1.sketch.wireOp",EDGE,"cbore_start_line_2")])]})}),subQ1,makeQuery(id+"F7.boolean.opBoolean","COPY",FACE,{"derivedFrom":subQ0}),makeQuery(id+"F16.opExtrude","SWEPT_FACE",FACE,{"disambiguationData":[OSD([sQuery(id+"F15.wireOp",EDGE,"E42")])]}),makeQuery(id+"F16.opExtrude","SWEPT_FACE",FACE,{"disambiguationData":[OSD([sQuery(id+"F15.wireOp",EDGE,"E43")])]})])],"derivedFrom":makeQuery(id+"F7.boolean.opBoolean","INTERSECT",EDGE,{"derivedFrom":[subQ1,subQ0]})});}
            var Q5;
            {var subQ0=makeQuery(id+"F7.opExtrude","CAP_FACE",FACE,{"disambiguationData":[OSD([sQuery(id+"F6.wireOp",EDGE,"E25"),sQuery(id+"F6.wireOp",EDGE,"E26"),sQuery(id+"F6.wireOp",EDGE,"E27"),sQuery(id+"F6.wireOp",EDGE,"E28"),sQuery(id+"F6.wireOp",EDGE,"E29.0"),sQuery(id+"F6.wireOp",EDGE,"E29.1"),sQuery(id+"F6.wireOp",EDGE,"E29.2"),sQuery(id+"F6.wireOp",EDGE,"E29.3"),sQuery(id+"F6.wireOp",EDGE,"E30"),sQuery(id+"F6.wireOp",EDGE,"E31")])],"isStart":true});var subQ1=makeQuery(id+"F5.opExtrude","SWEPT_FACE",FACE,{"disambiguationData":[OSD([sQuery(id+"F4.wireOp",EDGE,"E22.2"),sQuery(id+"F4.wireOp",EDGE,"E22.3")])]});Q5=makeQuery(id+"F16.boolean.opBoolean","SPLIT",EDGE,{"disambiguationData":[TD([makeQuery(id+"F3.hole-0.boolean.opBoolean","COPY",FACE,{"derivedFrom":makeQuery(id+"F3.hole-0.opRevolve","SWEPT_FACE",FACE,{"disambiguationData":[OSD([sQuery(id+"F3.hole-0.sketch.wireOp",EDGE,"cbore_start_line_2")])]})}),subQ1,makeQuery(id+"F7.boolean.opBoolean","COPY",FACE,{"derivedFrom":subQ0}),makeQuery(id+"F14.opExtrude","CAP_FACE",FACE,{"disambiguationData":[OSD([sQuery(id+"F13.wireOp",EDGE,"E39"),sQuery(id+"F13.wireOp",EDGE,"E40")])],"isStart":false}),makeQuery(id+"F16.opExtrude","SWEPT_FACE",FACE,{"disambiguationData":[OSD([sQuery(id+"F15.wireOp",EDGE,"E42")])]})])],"derivedFrom":makeQuery(id+"F7.boolean.opBoolean","INTERSECT",EDGE,{"derivedFrom":[subQ1,subQ0]})});}
            var Q6;
            {var subQ0=makeQuery(id+"F7.opExtrude","CAP_FACE",FACE,{"disambiguationData":[OSD([sQuery(id+"F6.wireOp",EDGE,"E25"),sQuery(id+"F6.wireOp",EDGE,"E26"),sQuery(id+"F6.wireOp",EDGE,"E27"),sQuery(id+"F6.wireOp",EDGE,"E28"),sQuery(id+"F6.wireOp",EDGE,"E29.0"),sQuery(id+"F6.wireOp",EDGE,"E29.1"),sQuery(id+"F6.wireOp",EDGE,"E29.2"),sQuery(id+"F6.wireOp",EDGE,"E29.3"),sQuery(id+"F6.wireOp",EDGE,"E30"),sQuery(id+"F6.wireOp",EDGE,"E31")])],"isStart":false});var subQ1=makeQuery(id+"F5.opExtrude","SWEPT_FACE",FACE,{"disambiguationData":[OSD([sQuery(id+"F4.wireOp",EDGE,"E22.2"),sQuery(id+"F4.wireOp",EDGE,"E22.3")])]});Q6=makeQuery(id+"F16.boolean.opBoolean","SPLIT",EDGE,{"disambiguationData":[TD([makeQuery(id+"F3.hole-0.boolean.opBoolean","COPY",FACE,{"derivedFrom":makeQuery(id+"F3.hole-0.opRevolve","SWEPT_FACE",FACE,{"disambiguationData":[OSD([sQuery(id+"F3.hole-0.sketch.wireOp",EDGE,"cbore_start_line_2")])]})}),subQ1,makeQuery(id+"F7.boolean.opBoolean","COPY",FACE,{"derivedFrom":subQ0}),makeQuery(id+"F14.opExtrude","CAP_FACE",FACE,{"disambiguationData":[OSD([sQuery(id+"F13.wireOp",EDGE,"E39"),sQuery(id+"F13.wireOp",EDGE,"E40")])],"isStart":false}),makeQuery(id+"F16.opExtrude","SWEPT_FACE",FACE,{"disambiguationData":[OSD([sQuery(id+"F15.wireOp",EDGE,"E42")])]})])],"derivedFrom":makeQuery(id+"F7.boolean.opBoolean","INTERSECT",EDGE,{"derivedFrom":[subQ1,subQ0]})});}
            var Q7;
            Q7=makeQuery(id+"F14.opExtrude","CAP_EDGE",EDGE,{"disambiguationData":[OSD([sQuery(id+"F13.wireOp",EDGE,"E40")])],"isStart":false});
            var Q8;
            Q8=makeQuery(id+"F14.opExtrude","CAP_EDGE",EDGE,{"disambiguationData":[OSD([sQuery(id+"F13.wireOp",EDGE,"E40")])],"isStart":true});
            var Q9;
            Q9=makeQuery(id+"F7.boolean.opBoolean","INTERSECT",EDGE,{"derivedFrom":[makeQuery(id+"F5.opExtrude","SWEPT_FACE",FACE,{"disambiguationData":[OSD([sQuery(id+"F4.wireOp",EDGE,"E22.1")])]}),makeQuery(id+"F7.opExtrude","CAP_FACE",FACE,{"disambiguationData":[OSD([sQuery(id+"F6.wireOp",EDGE,"E25"),sQuery(id+"F6.wireOp",EDGE,"E26"),sQuery(id+"F6.wireOp",EDGE,"E27"),sQuery(id+"F6.wireOp",EDGE,"E28"),sQuery(id+"F6.wireOp",EDGE,"E29.0"),sQuery(id+"F6.wireOp",EDGE,"E29.1"),sQuery(id+"F6.wireOp",EDGE,"E29.2"),sQuery(id+"F6.wireOp",EDGE,"E29.3"),sQuery(id+"F6.wireOp",EDGE,"E30"),sQuery(id+"F6.wireOp",EDGE,"E31")])],"isStart":false})]});
            var Q10;
            Q10=makeQuery(id+"F7.boolean.opBoolean","INTERSECT",EDGE,{"derivedFrom":[makeQuery(id+"F5.opExtrude","SWEPT_FACE",FACE,{"disambiguationData":[OSD([sQuery(id+"F4.wireOp",EDGE,"E22.1")])]}),makeQuery(id+"F7.opExtrude","CAP_FACE",FACE,{"disambiguationData":[OSD([sQuery(id+"F6.wireOp",EDGE,"E25"),sQuery(id+"F6.wireOp",EDGE,"E26"),sQuery(id+"F6.wireOp",EDGE,"E27"),sQuery(id+"F6.wireOp",EDGE,"E28"),sQuery(id+"F6.wireOp",EDGE,"E29.0"),sQuery(id+"F6.wireOp",EDGE,"E29.1"),sQuery(id+"F6.wireOp",EDGE,"E29.2"),sQuery(id+"F6.wireOp",EDGE,"E29.3"),sQuery(id+"F6.wireOp",EDGE,"E30"),sQuery(id+"F6.wireOp",EDGE,"E31")])],"isStart":true})]});
            chamfer(context, id + "F21", {"entities" : qUnion([Q0, Q1, Q2, Q3, Q4, Q5, Q6, Q7, Q8, Q9, Q10]), "width" : 0.5 * mm});
        }
        {
            var Q0;
            Q0=makeQuery(id+"F9.boolean.opBoolean","MERGE",FACE,{"derivedFrom":[makeQuery(id+"F5.boolean.opBoolean","MERGE",FACE,{"derivedFrom":[makeQuery(id+"F1.opExtrude","SWEPT_FACE",FACE,{"disambiguationData":[OSD([sQuery(id+"F0.wireOp",EDGE,"E10")])]}),makeQuery(id+"F5.opExtrude","SWEPT_FACE",FACE,{"disambiguationData":[OSD([sQuery(id+"F4.wireOp",EDGE,"E18")])]})]}),makeQuery(id+"F9.opExtrude","CAP_FACE",FACE,{"disambiguationData":[OSD([sQuery(id+"F8.wireOp",EDGE,"E33"),sQuery(id+"F8.wireOp",EDGE,"E34")])],"isStart":true})]});
            var Q1;
            Q1=makeQuery(id+"F11.boolean.opBoolean","MERGE",FACE,{"derivedFrom":[makeQuery(id+"F5.boolean.opBoolean","MERGE",FACE,{"derivedFrom":[makeQuery(id+"F1.opExtrude","SWEPT_FACE",FACE,{"disambiguationData":[OSD([sQuery(id+"F0.wireOp",EDGE,"E11")])]}),makeQuery(id+"F5.opExtrude","SWEPT_FACE",FACE,{"disambiguationData":[OSD([sQuery(id+"F4.wireOp",EDGE,"E23")])]})]}),makeQuery(id+"F11.opExtrude","CAP_FACE",FACE,{"disambiguationData":[OSD([sQuery(id+"F10.wireOp",EDGE,"E36"),sQuery(id+"F10.wireOp",EDGE,"E37")])],"isStart":true})]});
            chamfer(context, id + "F22", {"entities" : qUnion([Q0, Q1]), "width" : 0.5 * mm, "tangentPropagation" : true});
        }
        {
            var Q0;
            {var subQ0=sQuery(id+"F0.wireOp",EDGE,"E11");var subQ1=sQuery(id+"F0.wireOp",EDGE,"E7");Q0=makeQuery(id+"F20.opChamfer","BLEND_EDGE",EDGE,{"blendedFrom":[makeQuery(id+"F1.opExtrude","SWEPT_EDGE",EDGE,{"disambiguationData":[OSD([subQ1,subQ0])]}),makeQuery(id+"F5.boolean.opBoolean","MERGE",FACE,{"derivedFrom":[makeQuery(id+"F1.opExtrude","CAP_FACE",FACE,{"disambiguationData":[OSD([sQuery(id+"F0.wireOp",EDGE,"E5"),sQuery(id+"F0.wireOp",EDGE,"E6"),subQ1,sQuery(id+"F0.wireOp",EDGE,"E8"),sQuery(id+"F0.wireOp",EDGE,"E9.0"),sQuery(id+"F0.wireOp",EDGE,"E9.1"),sQuery(id+"F0.wireOp",EDGE,"E9.2"),sQuery(id+"F0.wireOp",EDGE,"E9.3"),sQuery(id+"F0.wireOp",EDGE,"E10"),subQ0])],"isStart":false}),makeQuery(id+"F5.opExtrude","CAP_FACE",FACE,{"disambiguationData":[OSD([sQuery(id+"F4.wireOp",EDGE,"E17"),sQuery(id+"F4.wireOp",EDGE,"E18"),sQuery(id+"F4.wireOp",EDGE,"E19"),sQuery(id+"F4.wireOp",EDGE,"E20"),sQuery(id+"F4.wireOp",EDGE,"E21"),sQuery(id+"F4.wireOp",EDGE,"E22.0"),sQuery(id+"F4.wireOp",EDGE,"E22.1"),sQuery(id+"F4.wireOp",EDGE,"E22.2"),sQuery(id+"F4.wireOp",EDGE,"E22.3"),sQuery(id+"F4.wireOp",EDGE,"E23")])],"isStart":false})]})],"blendedInto":[makeQuery(id+"F5.boolean.opBoolean","MERGE",FACE,{"derivedFrom":[makeQuery(id+"F1.opExtrude","CAP_FACE",FACE,{"disambiguationData":[OSD([sQuery(id+"F0.wireOp",EDGE,"E5"),sQuery(id+"F0.wireOp",EDGE,"E6"),subQ1,sQuery(id+"F0.wireOp",EDGE,"E8"),sQuery(id+"F0.wireOp",EDGE,"E9.0"),sQuery(id+"F0.wireOp",EDGE,"E9.1"),sQuery(id+"F0.wireOp",EDGE,"E9.2"),sQuery(id+"F0.wireOp",EDGE,"E9.3"),sQuery(id+"F0.wireOp",EDGE,"E10"),subQ0])],"isStart":false}),makeQuery(id+"F5.opExtrude","CAP_FACE",FACE,{"disambiguationData":[OSD([sQuery(id+"F4.wireOp",EDGE,"E17"),sQuery(id+"F4.wireOp",EDGE,"E18"),sQuery(id+"F4.wireOp",EDGE,"E19"),sQuery(id+"F4.wireOp",EDGE,"E20"),sQuery(id+"F4.wireOp",EDGE,"E21"),sQuery(id+"F4.wireOp",EDGE,"E22.0"),sQuery(id+"F4.wireOp",EDGE,"E22.1"),sQuery(id+"F4.wireOp",EDGE,"E22.2"),sQuery(id+"F4.wireOp",EDGE,"E22.3"),sQuery(id+"F4.wireOp",EDGE,"E23")])],"isStart":false})]})]});}
            var Q1;
            Q1=makeQuery(id+"F1.opExtrude","CAP_EDGE",EDGE,{"disambiguationData":[OSD([sQuery(id+"F0.wireOp",EDGE,"E6")])],"isStart":false});
            var Q2;
            {var subQ0=sQuery(id+"F0.wireOp",EDGE,"E11");var subQ1=sQuery(id+"F0.wireOp",EDGE,"E7");Q2=makeQuery(id+"F20.opChamfer","BLEND_EDGE",EDGE,{"blendedFrom":[makeQuery(id+"F1.opExtrude","SWEPT_EDGE",EDGE,{"disambiguationData":[OSD([subQ1,subQ0])]}),makeQuery(id+"F5.boolean.opBoolean","MERGE",FACE,{"derivedFrom":[makeQuery(id+"F1.opExtrude","CAP_FACE",FACE,{"disambiguationData":[OSD([sQuery(id+"F0.wireOp",EDGE,"E5"),sQuery(id+"F0.wireOp",EDGE,"E6"),subQ1,sQuery(id+"F0.wireOp",EDGE,"E8"),sQuery(id+"F0.wireOp",EDGE,"E9.0"),sQuery(id+"F0.wireOp",EDGE,"E9.1"),sQuery(id+"F0.wireOp",EDGE,"E9.2"),sQuery(id+"F0.wireOp",EDGE,"E9.3"),sQuery(id+"F0.wireOp",EDGE,"E10"),subQ0])],"isStart":true}),makeQuery(id+"F5.opExtrude","CAP_FACE",FACE,{"disambiguationData":[OSD([sQuery(id+"F4.wireOp",EDGE,"E17"),sQuery(id+"F4.wireOp",EDGE,"E18"),sQuery(id+"F4.wireOp",EDGE,"E19"),sQuery(id+"F4.wireOp",EDGE,"E20"),sQuery(id+"F4.wireOp",EDGE,"E21"),sQuery(id+"F4.wireOp",EDGE,"E22.0"),sQuery(id+"F4.wireOp",EDGE,"E22.1"),sQuery(id+"F4.wireOp",EDGE,"E22.2"),sQuery(id+"F4.wireOp",EDGE,"E22.3"),sQuery(id+"F4.wireOp",EDGE,"E23")])],"isStart":true})]})],"blendedInto":[makeQuery(id+"F5.boolean.opBoolean","MERGE",FACE,{"derivedFrom":[makeQuery(id+"F1.opExtrude","CAP_FACE",FACE,{"disambiguationData":[OSD([sQuery(id+"F0.wireOp",EDGE,"E5"),sQuery(id+"F0.wireOp",EDGE,"E6"),subQ1,sQuery(id+"F0.wireOp",EDGE,"E8"),sQuery(id+"F0.wireOp",EDGE,"E9.0"),sQuery(id+"F0.wireOp",EDGE,"E9.1"),sQuery(id+"F0.wireOp",EDGE,"E9.2"),sQuery(id+"F0.wireOp",EDGE,"E9.3"),sQuery(id+"F0.wireOp",EDGE,"E10"),subQ0])],"isStart":true}),makeQuery(id+"F5.opExtrude","CAP_FACE",FACE,{"disambiguationData":[OSD([sQuery(id+"F4.wireOp",EDGE,"E17"),sQuery(id+"F4.wireOp",EDGE,"E18"),sQuery(id+"F4.wireOp",EDGE,"E19"),sQuery(id+"F4.wireOp",EDGE,"E20"),sQuery(id+"F4.wireOp",EDGE,"E21"),sQuery(id+"F4.wireOp",EDGE,"E22.0"),sQuery(id+"F4.wireOp",EDGE,"E22.1"),sQuery(id+"F4.wireOp",EDGE,"E22.2"),sQuery(id+"F4.wireOp",EDGE,"E22.3"),sQuery(id+"F4.wireOp",EDGE,"E23")])],"isStart":true})]})]});}
            var Q3;
            Q3=makeQuery(id+"F1.opExtrude","CAP_EDGE",EDGE,{"disambiguationData":[OSD([sQuery(id+"F0.wireOp",EDGE,"E6")])],"isStart":true});
            chamfer(context, id + "F23", {"entities" : qUnion([Q0, Q1, Q2, Q3]), "width" : 0.5 * mm, "tangentPropagation" : true});
        }
        {
            var Q0;
            Q0=qCreatedBy(makeId("Front.planeOp"),FACE);
            var sketch = newSketch(context, id + "F24", { "sketchPlane" : qUnion([Q0])});
            skLineSegment(sketch, "E49", {"start": v(0, 0) * mm, "end": v(-12.5, 0) * mm, "construction": true});
            skLineSegment(sketch, "E50", {"start": v(-12.5, 0) * mm, "end": v(-12.5, 4.5) * mm});
            skLineSegment(sketch, "E51", {"start": v(-10, 7) * mm, "end": v(76.79, 7) * mm});
            skLineSegment(sketch, "E52", {"start": v(79.29, 4.5) * mm, "end": v(79.29, -4.5) * mm});
            skLineSegment(sketch, "E53", {"start": v(76.79, -7) * mm, "end": v(-10, -7) * mm});
            skLineSegment(sketch, "E54", {"start": v(-12.5, -4.5) * mm, "end": v(-12.5, 0) * mm});
            skPoint(sketch, "E55.visualSharp", {"position": v(-12.5, 7) * mm});
            skArc(sketch, "E55.filletArc", {"start": v(-10, 7) * mm, "mid": v(-11.77, 6.27) * mm, "end": v(-12.5, 4.5) * mm});
            skPoint(sketch, "E56.visualSharp", {"position": v(-12.5, -7) * mm});
            skArc(sketch, "E56.filletArc", {"start": v(-12.5, -4.5) * mm, "mid": v(-11.77, -6.27) * mm, "end": v(-10, -7) * mm});
            skPoint(sketch, "E57.visualSharp", {"position": v(79.29, 7) * mm});
            skArc(sketch, "E57.filletArc", {"start": v(79.29, 4.5) * mm, "mid": v(78.56, 6.27) * mm, "end": v(76.79, 7) * mm});
            skPoint(sketch, "E58.visualSharp", {"position": v(79.29, -7) * mm});
            skArc(sketch, "E58.filletArc", {"start": v(76.79, -7) * mm, "mid": v(78.56, -6.27) * mm, "end": v(79.29, -4.5) * mm});
            skSolve(sketch);
        }
        {
            var Q0;
            Q0 = qSketchRegion(id + "F24", true);
            extrude(context, id + "F25", {"entities" : qUnion([Q0]), "operationType" : NewBodyOperationType.ADD, "oppositeDirection" : true, "depth" : 3 * mm});
        }
        {
            var Q0;
            Q0=makeQuery(id+"F25.opExtrude","CAP_EDGE",EDGE,{"disambiguationData":[OSD([sQuery(id+"F24.wireOp",EDGE,"E58.filletArc")])],"isStart":false});
            chamfer(context, id + "F26", {"entities" : qUnion([Q0]), "width" : 2.5 * mm, "tangentPropagation" : true});
        }
        {
            var Q0;
            Q0=qCreatedBy(makeId("Front.planeOp"),FACE);
            var sketch = newSketch(context, id + "F27", { "sketchPlane" : qUnion([Q0])});
            skCircle(sketch, "E59", {"center": v(0, 0) * mm, "radius": 1.65 * mm});
            skLineSegment(sketch, "E60", {"start": v(0, 0) * mm, "end": v(40, 0) * mm, "construction": true});
            skCircle(sketch, "E61", {"center": v(40, 0) * mm, "radius": 1.65 * mm});
            skSolve(sketch);
        }
        {
            var Q0;
            Q0 = qSketchRegion(id + "F27", true);
            extrude(context, id + "F28", {"entities" : qUnion([Q0]), "operationType" : NewBodyOperationType.REMOVE, "endBound" : BoundingType.THROUGH_ALL, "oppositeDirection" : true, "depth" : 25 * mm});
        }
    });
